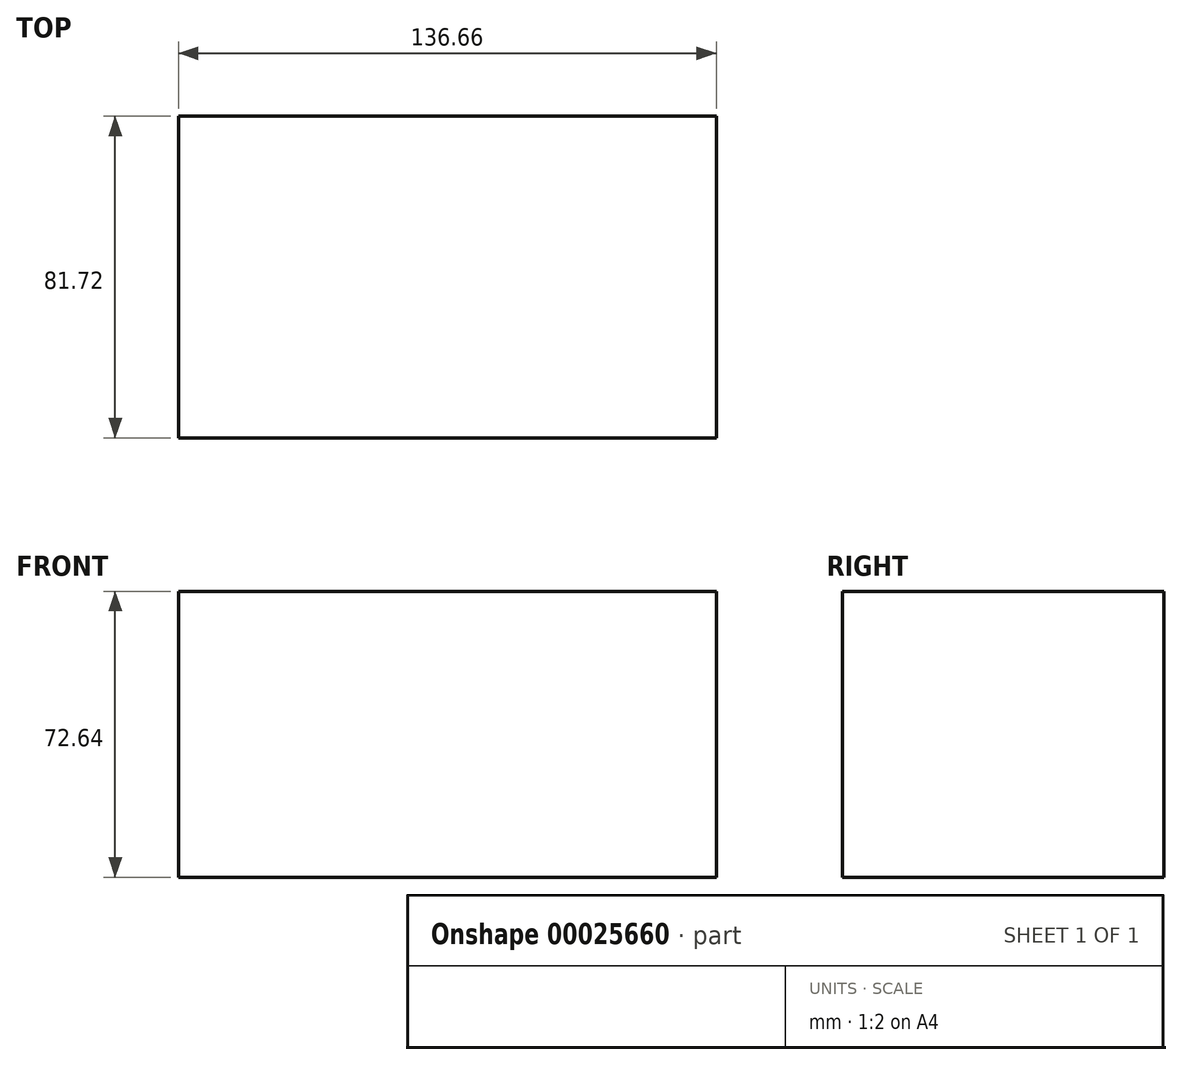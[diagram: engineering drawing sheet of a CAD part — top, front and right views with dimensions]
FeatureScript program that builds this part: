
annotation { "Feature Type Name" : "Feature", "Feature Type Description" : "" }
export const myFeature = defineFeature(function(context is Context, id is Id, definition is map)
    precondition{}
    {
        {
            var Q0;
            Q0=qCreatedBy(makeId("Top.planeOp"),FACE);
            var sketch = newSketch(context, id + "F0", { "sketchPlane" : qUnion([Q0])});
            skLineSegment(sketch, "E0.bottom", {"start": v(0, 0) * mm, "end": v(136.66, 0) * mm});
            skLineSegment(sketch, "E0.top", {"start": v(0, -81.72) * mm, "end": v(136.66, -81.72) * mm});
            skLineSegment(sketch, "E0.left", {"start": v(0, 0) * mm, "end": v(0, -81.72) * mm});
            skLineSegment(sketch, "E0.right", {"start": v(136.66, 0) * mm, "end": v(136.66, -81.72) * mm});
            skSolve(sketch);
        }
        {
            var Q0;
            Q0=makeQuery(id+"F0.imprint","IMPRINT",FACE,{"disambiguationData":[TD([[makeQuery(id+"F0.imprint","IMPRINT",EDGE,{"derivedFrom":sQuery(id+"F0.wireOp",EDGE,"E0.bottom")}),-1.0]])]});
            extrude(context, id + "F1", {"entities" : qUnion([Q0]), "depth" : 72.64 * mm});
        }
    });
